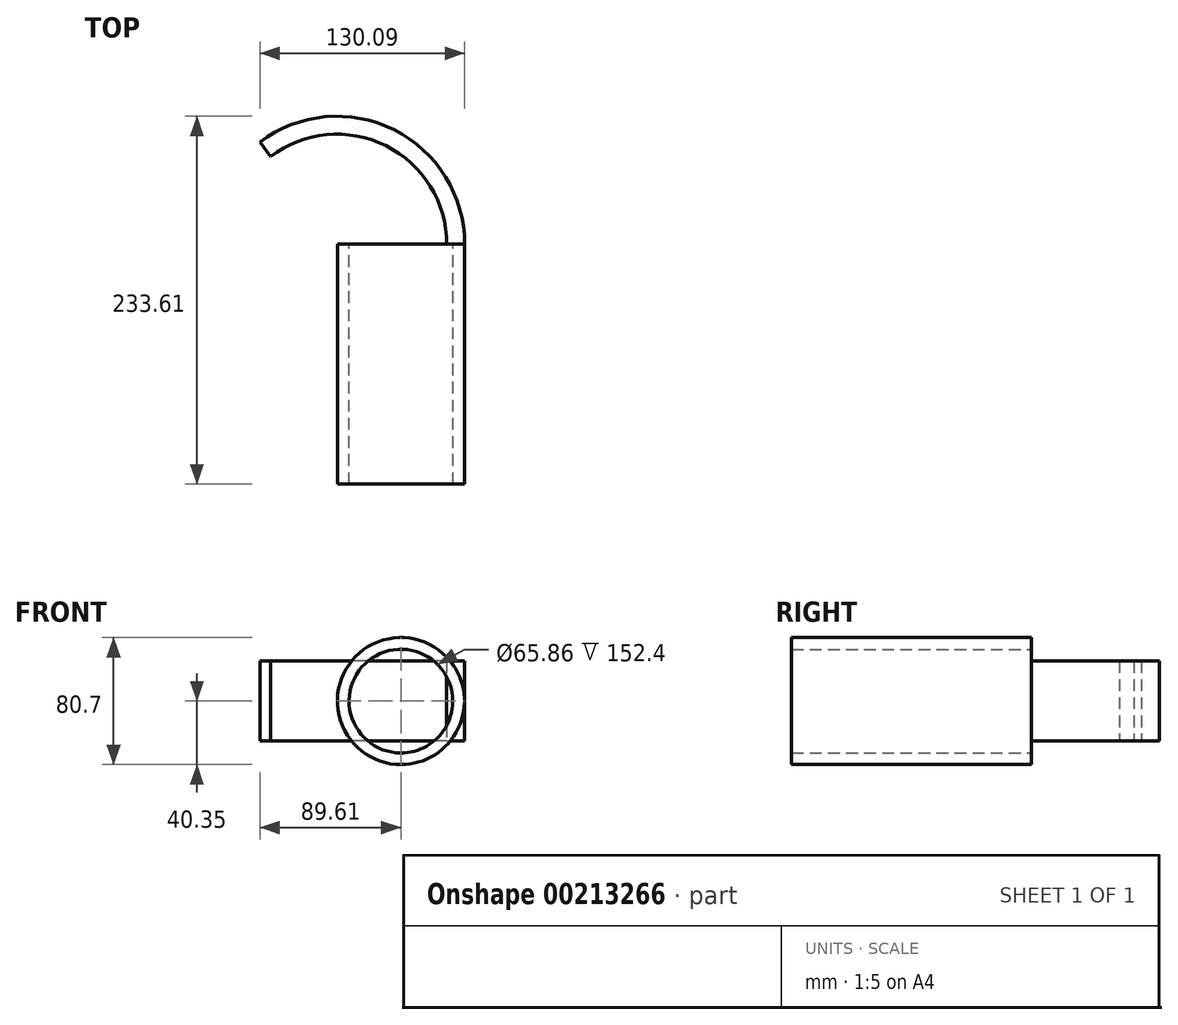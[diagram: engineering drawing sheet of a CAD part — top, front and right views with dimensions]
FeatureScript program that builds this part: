
annotation { "Feature Type Name" : "Feature", "Feature Type Description" : "" }
export const myFeature = defineFeature(function(context is Context, id is Id, definition is map)
    precondition{}
    {
        {
            var Q0;
            Q0=qCreatedBy(makeId("Front.planeOp"),FACE);
            var sketch = newSketch(context, id + "F0", { "sketchPlane" : qUnion([Q0])});
            skCircle(sketch, "E0", {"center": v(0, 0) * mm, "radius": 32.93 * mm});
            skCircle(sketch, "E1", {"center": v(0, 0) * mm, "radius": 40.35 * mm});
            skSolve(sketch);
        }
        {
            var Q0;
            Q0=makeQuery(id+"F0.imprint","IMPRINT",FACE,{"disambiguationData":[TD([[makeQuery(id+"F0.imprint","IMPRINT",EDGE,{"derivedFrom":sQuery(id+"F0.wireOp",EDGE,"E0")}),-1.0]])]});
            extrude(context, id + "F1", {"entities" : qUnion([Q0]), "depth" : 152.4 * mm});
        }
        {
            var Q0;
            Q0=qCreatedBy(makeId("Top.planeOp"),FACE);
            var sketch = newSketch(context, id + "F2", { "sketchPlane" : qUnion([Q0])});
            skCircle(sketch, "E2", {"center": v(-40.73, 0) * mm, "radius": 81.21 * mm});
            skCircle(sketch, "E3", {"center": v(-40.73, 0) * mm, "radius": 69.83 * mm});
            skLineSegment(sketch, "E4", {"start": v(-40.73, 0) * mm, "end": v(-121.69, 107.43) * mm, "construction": true});
            skLineSegment(sketch, "E5", {"start": v(-40.73, 0) * mm, "end": v(-40.73, 134.37) * mm, "construction": true});
            skLineSegment(sketch, "E6", {"start": v(-89.6, 64.86) * mm, "end": v(-82.75, 55.77) * mm});
            skLineSegment(sketch, "E7", {"start": v(29.1, 0) * mm, "end": v(40.48, 0) * mm});
            skSolve(sketch);
        }
        {
            var Q0;
            {var subQ0=sQuery(id+"F2.wireOp",EDGE,"E6");Q0=makeQuery(id+"F2.imprint","IMPRINT",FACE,{"disambiguationData":[TD([[makeQuery(id+"F2.imprint","IMPRINT",EDGE,{"derivedFrom":subQ0}),1.0]])]});}
            extrude(context, id + "F3", {"entities" : qUnion([Q0]), "operationType" : NewBodyOperationType.ADD, "depth" : 25.4 * mm, "hasSecondDirection" : true, "secondDirectionOppositeDirection" : true, "secondDirectionDepth" : 25.4 * mm});
        }
    });
